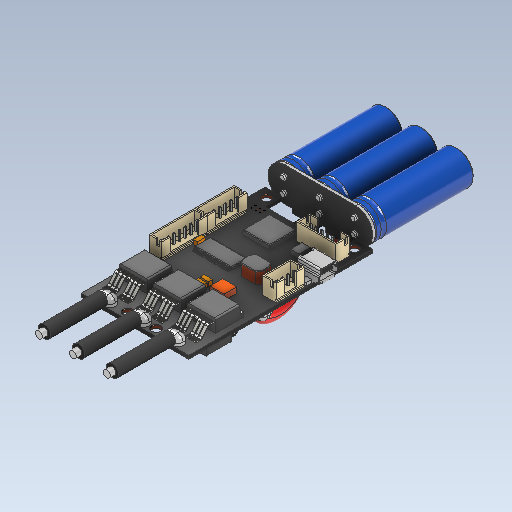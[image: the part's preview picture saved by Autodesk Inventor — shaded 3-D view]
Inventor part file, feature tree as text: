
AUTODESK INVENTOR PART (.ipt)
format: ipt  version: 2020.1 (Build 241239000, 239)  size: 2,892,288 bytes
history: native  units: mm
features: extrude x36, sketch x28, fillet x15, plane x11, pattern_linear x10, projected_geometry x7, sweep x5, chamfer x4, mirror x4, other x3, draft x2, revolve x2, pattern_circular x1
ambient origin geometry x8: Origin, YZ Plane, XZ Plane, XY Plane, X Axis, Y Axis, Z Axis, Center Point
bodies: Solid1 (feature_tree)
feature tree (128):
  sketch  "Sketch1"  dims[d0=38.0mm d1=65.0mm]
  extrude  "Extrusion1"  Depth=65.0mm
  extrude  "Extrusion4"  Depth=6.0mm
  extrude  "Extrusion5"  Depth=6.0mm
  extrude  "Extrusion6"  Depth=3.0mm
  extrude  "Extrusion7"  Depth=1.2mm TaperAngle=0.0deg
  extrude  "Extrusion8"  Depth=3.0mm
  extrude  "Extrusion10"  Depth=2.5mm
  extrude  "Extrusion12"  Depth=40.0mm
  extrude  "Extrusion13"  Depth=0.5mm
  extrude  "Extrusion14"  Depth=0.5mm
  extrude  "Extrusion15"  Depth=0.5mm
  extrude  "Extrusion16"  Depth=3.0mm
  extrude  "Extrusion17"  Depth=3.0mm
  extrude  "Extrusion18"  Depth=0.5mm
  extrude  "Extrusion19"  Depth=0.5mm
  extrude  "Extrusion20"  Depth=10.0mm
  extrude  "Extrusion21"  Depth=0.5mm
  fillet  "Fillet1"  Radius=1.8mm
  sketch  "Sketch6"  dims[d11=3.0mm d12=5.0mm]
  extrude  "Extrusion22"  Depth=5.5mm
  extrude  "Extrusion23"  Depth=2.0mm
  fillet  "Fillet2"  Radius=9.5mm
  fillet  "Fillet3"  Radius=9.5mm
  extrude  "Extrusion24"  Depth=3.0mm
  fillet  "Fillet4"  Radius=14.0mm
  extrude  "Extrusion25"  Depth=0.05mm
  chamfer  "Chamfer1"  Distance=0.5mm
  fillet  "Fillet5"  Radius=0.5mm
  chamfer  "Chamfer2"  Distance=0.5mm
  fillet  "Fillet6"  Radius=1.8mm
  draft  "FaceDraft1"
  plane  "Work Plane1"
  sketch  "Sketch10"  dims[d20=0.5mm d21=0.5mm]
  extrude  "Extrusion32"  Depth=10.0mm
  fillet  "Fillet14"  Radius=1.8mm
  pattern_linear  "Rectangular Pattern6"  Spacing1=10.0mm  [1 undecoded]
  sweep  "Sweep1"
  fillet  "Fillet7"  Radius=2.0mm
  plane  "Work Plane2"
  pattern_linear  "Rectangular Pattern1"  Spacing1=1.5mm  [1 undecoded]
  mirror  "Mirror1"
  pattern_linear  "Rectangular Pattern2"  Spacing1=2.5mm  [1 undecoded]
  sketch  "Sketch11"  dims[d23=0.5mm d24=0.5mm d25=0.5mm d26=0.5mm]
  plane  "Work Plane3"
  sweep  "Sweep2"
  fillet  "Fillet8"  Radius=2.0mm
  pattern_linear  "Rectangular Pattern3"  Spacing1=0.05mm  [1 undecoded]
  plane  "Work Plane4"
  mirror  "Mirror2"
  sketch  "Sketch13"  dims[d29=3.0mm d30=3.0mm]
  extrude  "Extrusion26"  Depth=0.05mm
  extrude  "Extrusion27"  Depth=4.0mm
  draft  "FaceDraft2"
  fillet  "Fillet9"  Radius=10.0mm
  extrude  "Extrusion28"  Depth=2.0mm
  fillet  "Fillet10"  Radius=11.0mm
  extrude  "Extrusion29"  Depth=0.5mm
  fillet  "Fillet11"  Radius=8.0mm
  extrude  "Extrusion30"  Depth=0.05mm
  fillet  "Fillet12"  Radius=2.0mm
  extrude  "Extrusion31"  Depth=0.5mm
  mirror  "Mirror3"
  sketch  "Sketch16"  dims[d35=70.0mm d37=1.98mm d38=10.0mm d40=10.0mm d56=1.935mm]
  plane  "Work Plane5"
  sweep  "Sweep3"
  fillet  "Fillet13"  Radius=0.5mm
  pattern_linear  "Rectangular Pattern4"  Spacing1=2.0mm  [1 undecoded]
  plane  "Work Plane6"
  mirror  "Mirror4"
  pattern_linear  "Rectangular Pattern5"  Spacing1=2.0mm  [1 undecoded]
  extrude  "Extrusion33"  Depth=1.0mm
  fillet  "Fillet15"  Radius=10.0mm
  pattern_linear  "Rectangular Pattern7"  Spacing1=5.0mm  [1 undecoded]
  revolve  "Revolution1"  [1 undecoded]
  pattern_linear  "Rectangular Pattern8"  Spacing1=0.5mm  [1 undecoded]
  plane  "Work Plane11"
  extrude  "Extrusion35"  Depth=0.5mm
  revolve  "Revolution2"  [1 undecoded]
  extrude  "Extrusion36"  Depth=3.0mm
  chamfer  "Chamfer3"  Distance=0.5mm
  chamfer  "Chamfer4"  Distance=0.5mm
  pattern_linear  "Rectangular Pattern9"  Spacing1=0.5mm  [1 undecoded]
  plane  "Work Plane12"
  extrude  "Extrusion37"  Depth=0.5mm
  other  "Work Axis1"
  pattern_circular  "Circular Pattern1"  [2 undecoded]
  pattern_linear  "Rectangular Pattern10"  Count1=4 Spacing1=1.98mm
  sketch  "Sketch29"  dims[d80=2.0mm]
  plane  "Work Plane13"
  plane  "Work Plane14"
  sketch  "Sketch30"  dims[d81=0.5mm]
  sketch  "Sketch31"  dims[d82=3.0mm]
  sketch  "3D Sketch2"
  plane  "Work Plane15"
  sketch  "Sketch32"  dims[d83=3.0mm]
  sweep  "Sweep6"
  sweep  "Sweep7"
  extrude  "Extrusion38"  Depth=0.5mm
  extrude  "Extrusion39"  Depth=0.5mm
  extrude  "Extrusion40"  Depth=0.05mm
  extrude  "Extrusion41"  Depth=0.05mm
  sketch  "Sketch33"  dims[d84=0.5mm d85=0.5mm d86=0.5mm d87=0.5mm d88=1.8mm d89=60.0mm d91=1.98mm d92=10.0mm d94=10.0mm d96=1.8mm d97=10.0mm d98=10.0mm d99=2.0mm d100=1.5mm d101=2.5mm d102=30.0mm d104=12.0mm d105=10.0mm d107=10.0mm d109=2.0mm d110=0.05mm d111=6.0mm d112=4.0mm d113=30.0mm d115=12.0mm d116=10.0mm d118=10.0mm d120=2.0mm d121=11.0mm d122=0.5mm d123=1.0mm d124=8.0mm d125=7.0mm d126=2.0mm d127=0.5mm d128=0.5mm d129=0.5mm d130=2.0mm d131=2.0mm d132=1.0mm d133=10.0mm d134=5.0mm d135=0.5mm d136=0.5mm d137=0.5mm d138=3.0mm d139=3.0mm d140=0.5mm d141=0.5mm d142=0.5mm d143=0.5mm d144=1.78mm d145=40.0mm d147=1.98mm d148=10.0mm d150=10.0mm d152=1.78mm d153=7.5mm d154=0.5mm d155=0.5mm d156=3.75mm d157=3.75mm d158=6.0mm d159=3.75mm d160=3.75mm d161=3.75mm d162=3.75mm d164=5.0mm d165=4.5mm d178=1.5mm d179=1.5mm d180=3.0mm d185=1.5mm d186=1.5mm d188=1.5mm d189=1.0mm d190=1.5mm d191=0.5mm d192=3.0mm d193=4.0mm d194=1.0mm d195=3.0mm d206=0.5mm d207=0.05mm d208=1.8mm d209=1.0mm d210=0.0mm d211=1.5mm d212=0.0mm d213=2.0mm d214=0.0mm d215=3.0mm d216=0.0mm d217=5.0mm d218=0.0mm d221=5.0mm d222=0.0mm d225=6.0mm d226=0.0mm d227=1.0mm d228=0.0mm d229=3.0mm d230=0.0mm d231=4.0mm d232=0.0mm d233=4.5mm d234=0.0mm d235=1.0mm d236=1.0mm d237=1.0mm d238=1.0mm d239=1.0mm d240=1.0mm d241=2.0mm d242=0.0mm d243=0.3mm d244=0.3mm d245=0.3mm d246=0.3mm d247=1.5mm d248=0.0mm d249=0.05mm d250=0.5mm d251=0.5mm d252=0.5mm d253=2.0mm d254=0.0mm d255=0.5mm d256=0.5mm d257=0.5mm d258=2.0mm d259=0.0mm d260=0.5mm d261=0.5mm d262=0.5mm d263=2.0mm d264=0.0mm d265=0.5mm d266=0.3mm d267=1.0mm d268=1.0mm d269=6.5mm d270=0.0mm d271=0.7mm d272=0.7mm d273=0.0mm d274=0.3mm d275=0.5mm d276=45.0deg d277=135.0deg d279=1.5mm d280=4.5mm d281=1.0mm d282=5.5mm d283=0.0mm d284=0.2mm d285=0.7mm d286=0.5mm d287=0.5mm d288=3.5mm d289=0.55mm d290=0.55mm d291=7.0mm d292=0.0mm d293=0.2mm d294=2.0mm d295=45.0deg d296=0.5mm d297=0.2mm d298=2.0mm d299=45.0deg d300=2.0mm d301=1.22173mm d302=-0.5mm d311=2.0mm d312=0.4mm d313=0.0mm d314=0.0mm d315=1.0mm d316=3.0mm d317=2.0mm d318=1.0mm d319=3.0mm d320=1.0mm d321=0.5mm d322=30.0mm d324=1.34mm d325=30.0mm d327=12.0mm d328=0.1mm d329=0.1mm d330=0.5mm d331=0.1mm d332=-0.1mm d333=0.1mm d334=0.0mm d336=0.35mm d337=1.0mm d338=1.22173mm d339=0.0mm d340=0.0mm d341=0.5mm d342=280.0mm d344=0.47mm d345=10.0mm d346=10.0mm d348=12.0mm d349=1.5mm d350=2.0mm d351=2.0mm d352=2.0mm d353=2.0mm d354=10.0mm d355=7.0mm d356=7.0mm d357=7.0mm d358=6.0mm d359=8.5mm d360=6.0mm d361=5.0mm d362=0.2mm d363=2.0mm d364=4.0mm d365=6.0mm d366=1.0mm d367=1.0mm d368=0.0mm d369=4.5mm d370=0.0mm d371=1.22173mm d372=0.5mm d373=3.0mm d374=0.0mm d375=2.0mm d376=2.0mm d377=0.0mm d378=0.5mm d379=0.2mm d380=0.2mm d381=2.0mm d382=0.0mm d383=0.3mm d384=0.5mm d385=0.5mm d388=2.0mm d389=3.0mm d390=2.0mm d391=0.0mm d392=1.0mm d393=0.4mm d394=3.0mm d395=0.5mm d396=-0.5mm d397=2.0mm d398=1.0mm d399=3.0mm d400=2.0mm d401=0.0mm d402=0.0mm d403=1.0mm d404=30.0mm d406=1.34mm d407=30.0mm d409=12.0mm d410=1.0mm d411=2.0mm d412=0.0mm d413=1.0mm d414=30.0mm d416=12.0mm d417=1.0mm d418=2.0mm d419=0.0mm d420=1.0mm d421=30.0mm d423=12.0mm d424=2.25mm d425=20.0mm d426=1.0mm d427=30.543262mm d428=2.0mm d429=90.0deg d430=30.0mm d432=12.0mm d443=0.5mm d444=12.5mm d445=12.0mm d446=1.0mm d447=0.0mm d448=1.0mm d449=8.0mm d450=1.5mm d451=2.0mm d452=8.0mm d453=1.5mm d454=2.0mm d459=2.0mm d460=3.0mm d461=1.5mm d462=135.0deg d463=6.0mm d464=0.5mm d465=0.5mm d466=0.2mm d467=4.0mm d468=35.0mm d469=6.0mm d470=1.75mm d471=90.0deg d472=2.0mm d473=2.5mm d474=1.0mm d475=0.0mm d476=0.2mm d477=0.5mm d478=45.0deg d479=0.2mm d480=0.5mm d481=45.0deg d482=30.0mm d484=12.5mm d485=-0.1mm d488=0.3mm d489=30.0mm d491=360.0deg d493=5.0mm d494=0.0mm d495=30.0mm d496=360.0deg d498=30.0mm d500=12.5mm d501=2.0mm d502=2.25mm d504=4.5mm d506=2.48mm d507=0.0mm d508=0.0mm d509=0.0mm d510=0.0mm d511=40.0mm d512=0.0mm d513=38.0mm d514=0.0mm d518=2.5mm d519=1.0mm d520=0.8mm d522=0.0mm d523=2.0mm d524=30.0mm d526=1.5mm d527=10.0mm d529=10.0mm d531=0.05mm d532=0.0mm d533=0.05mm d534=0.0mm d536=1.24mm]
  sketch  "Sketch2"  dims[d2=6.0mm d3=6.0mm]
  projected_geometry  "Projected Loop1"
  projected_geometry  "Projected Loop2"
  projected_geometry  "Projected Loop3"
  sketch  "Sketch3"  dims[d4=6.0mm d5=6.0mm]
  sketch  "Sketch4"  dims[d6=3.0mm d7=3.5mm]
  sketch  "Sketch5"  dims[d8=3.0mm d9=1.2mm d10=0.0mm]
  sketch  "Sketch7"  dims[d13=2.5mm d14=24.0mm]
  sketch  "Sketch8"  dims[d15=54.05mm d16=40.0mm]
  sketch  "Sketch9"  dims[d18=4.5mm d19=0.5mm]
  sketch  "Sketch12"  dims[d27=3.0mm d28=3.0mm]
  projected_geometry  "Projected Loop4"
  sketch  "Sketch14"  dims[d31=0.5mm d32=0.5mm]
  projected_geometry  "Projected Loop5"
  sketch  "Sketch15"  dims[d33=0.5mm d34=1.935mm]
  sketch  "Sketch17"  dims[d58=0.5mm d59=0.5mm]
  projected_geometry  "Projected Loop6"
  sketch  "Sketch18"  dims[d61=60.0mm d63=1.98mm d64=10.0mm d66=10.0mm d68=1.8mm]
  sketch  "Sketch24"  dims[d69=13.0mm d70=5.5mm]
  sketch  "Sketch26"  dims[d71=2.0mm d72=7.5mm d73=9.5mm d74=9.5mm]
  sketch  "Sketch27"  dims[d75=3.0mm d76=6.0mm d77=14.0mm]
  projected_geometry  "Projected Loop14"
  sketch  "Sketch28"  dims[d78=0.05mm d79=5.0mm]
  other  "3D Intersection2"
  other  "3D Intersection3"
note: 13 required parameter values undecoded (feature->parameter linkage not recoverable at this tier; creation-order binding heuristic only, values carry confidence <= 0.55)